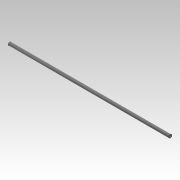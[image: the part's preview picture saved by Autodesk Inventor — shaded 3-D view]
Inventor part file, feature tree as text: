
AUTODESK INVENTOR PART (.ipt)
format: ipt  version: 2020 (Build 240168000, 168)  size: 90,112 bytes
history: native  units: mm
features: revolve x1, chamfer x1, sketch x1
ambient origin geometry x8: Origin, YZ Plane, XZ Plane, XY Plane, X Axis, Y Axis, Z Axis, Center Point
bodies: Solid1 (feature_tree)
feature tree (3):
  revolve  "Revolution1"  [1 undecoded]
  chamfer  "Chamfer1"  Distance=200.0mm
  sketch  "Sketch1"  dims[d0=1.0mm d1=2.0mm d2=200.0mm d3=90.0deg d4=0.25mm d5=2.0mm d6=45.0deg]
note: 1 required parameter value undecoded (feature->parameter linkage not recoverable at this tier; creation-order binding heuristic only, values carry confidence <= 0.55)
